# Revit family: Outlet-Bath-Caroma Quatro-Wall1
name_source: partatom
category: Plumbing Fixtures
revit_build: Autodesk Revit 2014 (Build: 20131024_2115(x64)
units: mm (PartAtom-declared; Revit-internal decimal feet)

## types (1)
- Standard
    Assembly Code = C1030210
    CW Connection = Yes
    CWFU = 4
    Connector Radius = 10 mm  [stored 0.0328084 ft]
    Cost = 0 $
    Default Elevation = 500 mm  [stored 1.64042 ft]
    Description = Effortlessly stylish and exceptionally functional, the new Quatro range is designed to impress. Contemporary and refined, this range incorporates loop style handles and a polished finish to ensure that your bathroom brings you peace of mind
    HW Connection = Yes
    HWFU = 4
    Manufacturer = GWA Bathrooms & Kitchens
    Material_ANZRS = Metal-Chrome-Caroma
    Model = 90709C
    ModifiedIssue_ANZRS = 20150121.01 $
    Type Comments = Caroma Quatro Bath Outlet
    URL = http://www.caroma.com.au
    Vent Connection = No
    Waste Connection = No

note: [stored X ft] marks values corroborated as IEEE doubles in the binary element streams (Revit-internal decimal feet)

## geometry (parser evidence)
native form markers: Blend x10, Sweep x1
no freeform markers — native parametric forms only
